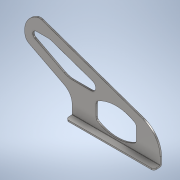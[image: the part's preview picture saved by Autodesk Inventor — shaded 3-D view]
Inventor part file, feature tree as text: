
AUTODESK INVENTOR PART (.ipt)
format: ipt  version: 2020 (Build 240168000, 168)  size: 260,096 bytes
history: native  units: mm
features: other x3, extrude x1
ambient origin geometry x8: Origin, YZ Plane, XZ Plane, XY Plane, X Axis, Y Axis, Z Axis, Center Point
bodies: Body1 (feature_tree)
feature tree (4):
  other  "實體1"
  extrude  "擠出1"  Depth=120.0mm
  other  "折彎零件1"
  other  "定義1"
